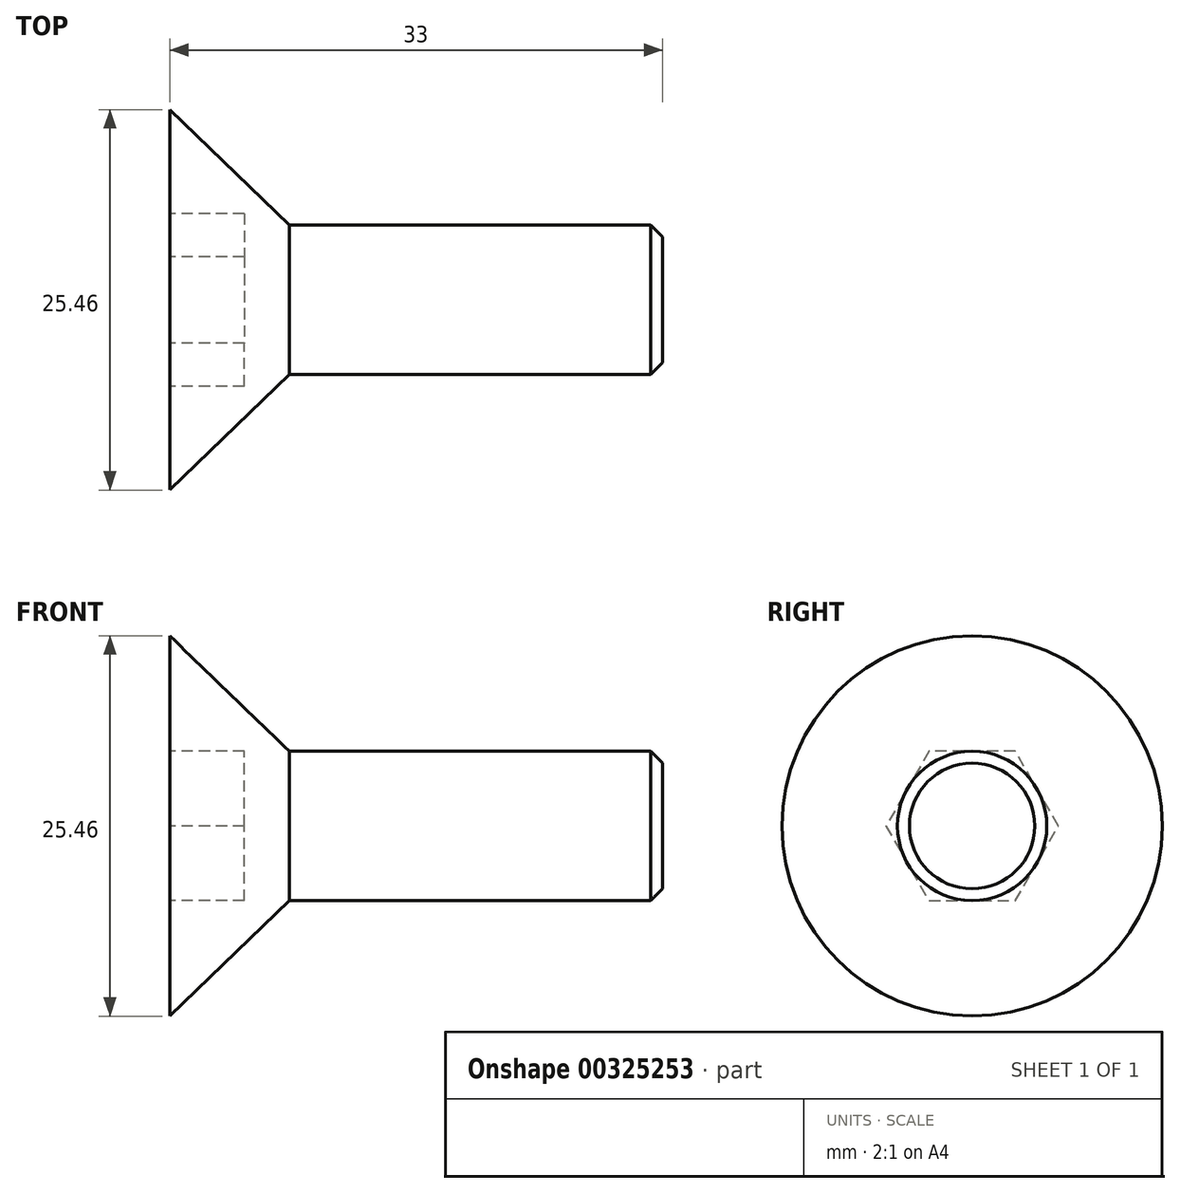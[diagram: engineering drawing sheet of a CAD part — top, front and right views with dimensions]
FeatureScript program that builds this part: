
annotation { "Feature Type Name" : "Feature", "Feature Type Description" : "" }
export const myFeature = defineFeature(function(context is Context, id is Id, definition is map)
    precondition{}
    {
        {
            var Q0;
            Q0=qCreatedBy(makeId("Front.planeOp"),FACE);
            var sketch = newSketch(context, id + "F0", { "sketchPlane" : qUnion([Q0])});
            skLineSegment(sketch, "E0", {"start": v(0, 12.73) * mm, "end": v(8, 5) * mm});
            skLineSegment(sketch, "E1", {"start": v(8, 5) * mm, "end": v(33, 5) * mm});
            skLineSegment(sketch, "E2", {"start": v(33, 5) * mm, "end": v(33, 0) * mm});
            skLineSegment(sketch, "E3", {"start": v(33, 0) * mm, "end": v(34.74, 0) * mm, "construction": true});
            skLineSegment(sketch, "E4", {"start": v(0, 0) * mm, "end": v(33, 0) * mm});
            skLineSegment(sketch, "E5", {"start": v(0, 12.73) * mm, "end": v(0, 0) * mm});
            skSolve(sketch);
        }
        {
            var Q0;
            Q0=makeQuery(id+"F0.imprint","IMPRINT",FACE,{"disambiguationData":[TD([[makeQuery(id+"F0.imprint","IMPRINT",EDGE,{"derivedFrom":sQuery(id+"F0.wireOp",EDGE,"E0")}),-1.0]])]});
            var Q1;
            Q1=sQuery(id+"F0.wireOp",EDGE,"E4");
            revolve(context, id + "F1", {"entities" : qUnion([Q0]), "axis" : qUnion([Q1]), "revolveType" : RevolveType.FULL});
        }
        {
            var Q0;
            Q0=makeQuery(id+"F1.opRevolve","SWEPT_FACE",FACE,{"disambiguationData":[OSD([sQuery(id+"F0.wireOp",EDGE,"E5")])]});
            var sketch = newSketch(context, id + "F2", { "sketchPlane" : qUnion([Q0])});
            skCircle(sketch, "E6.cCircle", {"center": v(0, 0) * mm, "radius": 5 * mm, "construction": true});
            skLineSegment(sketch, "E6.0", {"start": v(-2.89, 5) * mm, "end": v(2.89, 5) * mm});
            skLineSegment(sketch, "E6.1", {"start": v(2.89, 5) * mm, "end": v(5.77, 0) * mm});
            skLineSegment(sketch, "E6.2", {"start": v(5.77, 0) * mm, "end": v(2.89, -5) * mm});
            skLineSegment(sketch, "E6.3", {"start": v(2.89, -5) * mm, "end": v(-2.89, -5) * mm});
            skLineSegment(sketch, "E6.4", {"start": v(-2.89, -5) * mm, "end": v(-5.77, 0) * mm});
            skLineSegment(sketch, "E6.5", {"start": v(-5.77, 0) * mm, "end": v(-2.89, 5) * mm});
            skPoint(sketch, "E6.0.midPoint", {"position": v(0, 5) * mm});
            skSolve(sketch);
        }
        {
            var Q0;
            Q0=makeQuery(id+"F2.imprint","IMPRINT",FACE,{"disambiguationData":[TD([[makeQuery(id+"F2.imprint","IMPRINT",EDGE,{"derivedFrom":sQuery(id+"F2.wireOp",EDGE,"E6.0")}),-1.0]])]});
            extrude(context, id + "F3", {"entities" : qUnion([Q0]), "operationType" : NewBodyOperationType.REMOVE, "oppositeDirection" : true, "depth" : 5 * mm});
        }
        {
            var Q0;
            Q0=makeQuery(id+"F1.opRevolve","SWEPT_EDGE",EDGE,{"disambiguationData":[OSD([sQuery(id+"F0.wireOp",EDGE,"E1"),sQuery(id+"F0.wireOp",EDGE,"E2")])]});
            chamfer(context, id + "F4", {"entities" : qUnion([Q0]), "width" : 0.8 * mm, "tangentPropagation" : true});
        }
    });
